# Revit family: Pump_Commercial-Effluent-Zoeller-X6160-X6180_Vertical_Series
name_source: partatom
category: Mechanical Equipment
units: mm (PartAtom-declared; Revit-internal decimal feet)

## family parameters
Always vertical = No
Cut with Voids When Loaded = No
OmniClass Number = 23.60.30.21
OmniClass Title = Pumps
Part Type = Normal
Room Calculation Point = No
Round Connector Dimension = Use Radius
Shared = Yes
Work Plane-Based = Yes

## types (25) — shared parameters
Assembly Code = D2010900
Default Elevation = 0"
Description = Commercial Effluent Pumps for Class I, Division 1, Group C & D Locations
Discharge Diameter = 1 1/2"
Discharge Height = 6 1/16"
Discharge Radius = 3/4"
Height = 24 25/32"
Hertz = 60
Impeller Type = Bronze Vortex
Installation Type = Floor Mounted
Length = 13 5/16"
Manufacturer = Zoeller
Material = Cast Iron-Zoeller-Powder Coated Epoxy
Max. Water Temp. = 104 °F
Min. Recommended Fluid Level = 24"
Motor Design Letter = NEMA B
Motor Shaft = 416 S.S.
Motor Type = Submersible
Operation = Non-Automatic
Price = Prices may vary. Please consult Manufacturer Representative for most up-to-date price list.
Product Documentation Link = https://www.zoellerengineered.com
Product Page URL = https://www.zoellerengineered.com
RPM = 3450
Revised Date = 04/23/2024
Service Factor = 1.15
Shaft Seal Lower (Options) = Silicon Carbide/Carbon, Silicon Carbide/Silicon Carbide
Shaft Seal Lower Standard = Carbon/Silicon Carbide
Shaft Seal Upper Standard = Carbon/Ceramic
Shaft Seat Upper (Options) = Silicon Carbide/Carbon, Silicon Carbide/Silicon Carbide
Shipping Weight = 125-133 lbs
Square Ring Seals = Viton
Surface Temperature Code = T5 (1PH) T6 (3PH)
Tandem Seals = Standard
Type = Permanent Split Capacitor or 3 Phase
Type SOW Power Cord Length = 300"
URL = http://www.zoellerengprod.com
Warranty Information = 36 Months (Limited)
Waste Connection = Yes
Width = 8"

## per-type parameters (varying)
| type | Amps | Apparent Load | Flow | Insulation | Lead Wires Insulation | Max. Flow at Min. Head | Max. Stator Temp. | Maximum Head | Model | Motor | Motor Thermal Shutoff | Phase | Voltage |
| X6165-1.5"-3" 200V/1Ph/12.6A/1HP | 13 A | 2520 VA | 62 GPM | Class B | Class B | 62 GPM @ 5' | 266 °F | 86 1/2" | X6165 | 1 HP | Integral Overload With Automatic Reset - 1 Phase | 1 | 200 V |
| X6165-1.5"-3" 230V/1Ph/10.2A/1HP | 10 A | 2346 VA | 62 GPM | Class B | Class B | 62 GPM @ 5' | 266 °F | 86 1/2" | X6165 | 1 HP | Integral Overload With Automatic Reset - 1 Phase | 1 | 230 V |
| X6165-1.5"-3" 200V/3Ph/7.5A/1HP | 8 A | 1500 VA | 62 GPM | Class B | Class B | 62 GPM @ 5' | 266 °F | 86 1/2" | X6165 | 1 HP | Thermal Sensor With Lead Wires - 3 Phase | 3 | 200 V |
| X6165-1.5"-3" 230V/3Ph/7.4A/1HP | 7 A | 1702 VA | 62 GPM | Class B | Class B | 62 GPM @ 5' | 266 °F | 86 1/2" | X6165 | 1 HP | Thermal Sensor With Lead Wires - 3 Phase | 3 | 230 V |
| X6165-1.5"-3" 460V/3Ph/3.7A/1HP | 4 A | 1702 VA | 62 GPM | Class B | Class B | 62 GPM @ 5' | 266 °F | 86 1/2" | X6165 | 1 HP | Thermal Sensor With Lead Wires - 3 Phase | 3 | 460 V |
| X6185-1.5"-3" 200V/1Ph/11.5A/1HP | 12 A | 2300 VA | 85 GPM | Class B | Class B | 85 GPM @ 30' | 266 °F | 73" | X6185 | 1 HP | Integral Overload With Automatic Reset - 1 Phase | 1 | 200 V |
| X6185-1.5"-3" 230V/1Ph/9.8A/1HP | 10 A | 2254 VA | 85 GPM | Class B | Class B | 85 GPM @ 30' | 266 °F | 73" | X6185 | 1 HP | Integral Overload With Automatic Reset - 1 Phase | 1 | 230 V |
| X6185-1.5"-3" 200V/3Ph/7.5A/1HP | 8 A | 1500 VA | 85 GPM | Class B | Class B | 85 GPM @ 30' | 266 °F | 73" | X6185 | 1 HP | Thermal Sensor With Lead Wires - 3 Phase | 3 | 200 V |
| X6185-1.5"-3" 230V/3Ph/7.4A/1HP | 7 A | 1702 VA | 85 GPM | Class B | Class B | 85 GPM @ 30' | 266 °F | 73" | X6185 | 1 HP | Thermal Sensor With Lead Wires - 3 Phase | 3 | 230 V |
| X6185-1.5"-3" 460V/3Ph/3.7A/1HP | 4 A | 1702 VA | 85 GPM | Class B | Class B | 85 GPM @ 30' | 266 °F | 73" | X6185 | 1 HP | Thermal Sensor With Lead Wires - 3 Phase | 3 | 460 V |
| X6186-1.5"-3" 200V/1Ph/17.2A/1.5HP | 17 A | 3440 VA | 58 GPM | Class F | Class F | 58 GPM @ 5' | 311 °F | 114" | X6186 | 1.5 HP | Integral Overload With Automatic Reset - 1 Phase | 1 | 200 V |
| X6186-1.5"-3" 230V/1Ph/13.7A/1.5HP | 14 A | 3151 VA | 58 GPM | Class F | Class F | 58 GPM @ 5' | 311 °F | 114" | X6186 | 1.5 HP | Integral Overload With Automatic Reset - 1 Phase | 1 | 230 V |
| X6186-1.5"-3" 200V/3Ph/10.3A/1.5HP | 10 A | 2060 VA | 58 GPM | Class F | Class F | 58 GPM @ 5' | 311 °F | 114" | X6186 | 1.5 HP | Thermal Sensor With Lead Wires - 3 Phase | 3 | 200 V |
| X6186-1.5"-3" 230V/3Ph/9.2A/1.5HP | 9 A | 2116 VA | 58 GPM | Class F | Class F | 58 GPM @ 5' | 311 °F | 114" | X6186 | 1.5 HP | Thermal Sensor With Lead Wires - 3 Phase | 3 | 230 V |
| X6186-1.5"-3" 460V/3Ph/4.6A/1.5HP | 5 A | 2116 VA | 58 GPM | Class F | Class F | 58 GPM @ 5' | 311 °F | 114" | X6186 | 1.5 HP | Thermal Sensor With Lead Wires - 3 Phase | 3 | 460 V |
| X6188-1.5"-3" 200V/1Ph/16.8A/1.5HP | 17 A | 3360 VA | 145 GPM | Class F | Class F | 145 GPM @ 5' | 311 °F | 91" | X6188 | 1.5 HP | Integral Overload With Automatic Reset - 1 Phase | 1 | 200 V |
| X6188-1.5"-3" 230V/1Ph/14.0A/1.5HP | 14 A | 3220 VA | 145 GPM | Class F | Class F | 145 GPM @ 5' | 311 °F | 91" | X6188 | 1.5 HP | Integral Overload With Automatic Reset - 1 Phase | 1 | 230 V |
| X6188-1.5"-3" 200V/3Ph/10.3A/1.5HP | 10 A | 2060 VA | 145 GPM | Class F | Class F | 145 GPM @ 5' | 311 °F | 91" | X6188 | 1.5 HP | Thermal Sensor With Lead Wires - 3 Phase | 3 | 200 V |
| X6188-1.5"-3" 230V/3Ph/8.9A/1.5HP | 9 A | 2047 VA | 145 GPM | Class F | Class F | 145 GPM @ 5' | 311 °F | 91" | X6188 | 1.5 HP | Thermal Sensor With Lead Wires - 3 Phase | 3 | 230 V |
| X6188-1.5"-3" 460V/3Ph/4.6A/1.5HP | 5 A | 2116 VA | 145 GPM | Class F | Class F | 145 GPM @ 5' | 311 °F | 91" | X6188 | 1.5 HP | Thermal Sensor With Lead Wires - 3 Phase | 3 | 460 V |
| X6189-1.5"-3" 200V/1Ph/20.5A/2HP | 21 A | 4100 VA | 145 GPM | Class F | Class F | 145 GPM @ 5' | 311 °F | 110" | X6189 | 2 HP | Integral Overload With Automatic Reset - 1 Phase | 1 | 200 V |
| X6189-1.5"-3" 230V/1Ph/17.1A/2HP | 17 A | 3933 VA | 145 GPM | Class F | Class F | 145 GPM @ 5' | 311 °F | 110" | X6189 | 2 HP | Integral Overload With Automatic Reset - 1 Phase | 1 | 230 V |
| X6189-1.5"-3" 200V/3Ph/13.2A/2HP | 13 A | 2640 VA | 145 GPM | Class F | Class F | 145 GPM @ 5' | 311 °F | 110" | X6189 | 2 HP | Thermal Sensor With Lead Wires - 3 Phase | 3 | 200 V |
| X6189-1.5"-3" 230V/3Ph/11.2A/2HP | 11 A | 2576 VA | 145 GPM | Class F | Class F | 145 GPM @ 5' | 311 °F | 110" | X6189 | 2 HP | Thermal Sensor With Lead Wires - 3 Phase | 3 | 230 V |
| X6189-1.5"-3" 460V/3Ph/6.0A/2HP | 6 A | 2760 VA | 145 GPM | Class F | Class F | 145 GPM @ 5' | 311 °F | 110" | X6189 | 2 HP | Thermal Sensor With Lead Wires - 3 Phase | 3 | 460 V |

## geometry (parser evidence)
native form markers: Sweep x3
no freeform markers — native parametric forms only
